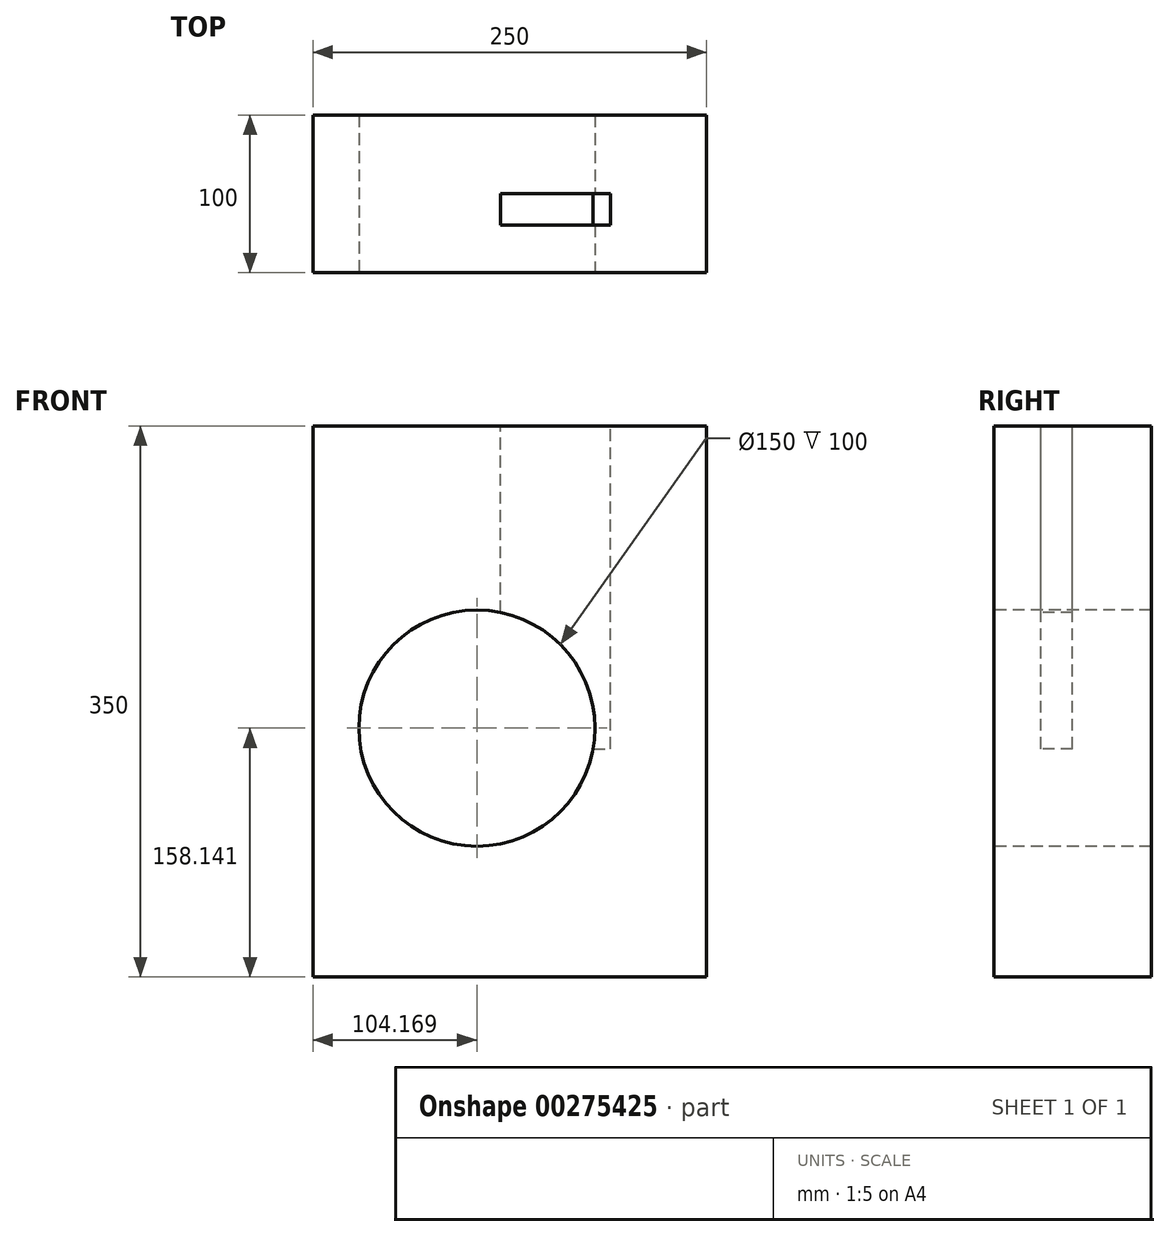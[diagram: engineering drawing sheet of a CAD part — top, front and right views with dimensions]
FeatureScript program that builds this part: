
annotation { "Feature Type Name" : "Feature", "Feature Type Description" : "" }
export const myFeature = defineFeature(function(context is Context, id is Id, definition is map)
    precondition{}
    {
        {
            var Q0;
            Q0=qCreatedBy(makeId("Front.planeOp"),FACE);
            var sketch = newSketch(context, id + "F0", { "sketchPlane" : qUnion([Q0])});
            skLineSegment(sketch, "E0.bottom", {"start": v(-125, 175) * mm, "end": v(125, 175) * mm});
            skLineSegment(sketch, "E0.top", {"start": v(-125, -175) * mm, "end": v(125, -175) * mm});
            skLineSegment(sketch, "E0.left", {"start": v(-125, 175) * mm, "end": v(-125, -175) * mm});
            skLineSegment(sketch, "E0.right", {"start": v(125, 175) * mm, "end": v(125, -175) * mm});
            skSolve(sketch);
        }
        {
            var Q0;
            Q0 = qSketchRegion(id + "F0", true);
            extrude(context, id + "F1", {"entities" : qUnion([Q0]), "depth" : 100 * mm});
        }
        {
            var Q0;
            Q0=makeQuery(id+"F1.opExtrude","CAP_FACE",FACE,{"disambiguationData":[OSD([sQuery(id+"F0.wireOp",EDGE,"E0.bottom"),sQuery(id+"F0.wireOp",EDGE,"E0.top"),sQuery(id+"F0.wireOp",EDGE,"E0.left"),sQuery(id+"F0.wireOp",EDGE,"E0.right")])],"isStart":false});
            var sketch = newSketch(context, id + "F2", { "sketchPlane" : qUnion([Q0])});
            skCircle(sketch, "E1", {"center": v(-20.83, -16.86) * mm, "radius": 75 * mm});
            skSolve(sketch);
        }
        {
            var Q0;
            Q0=makeQuery(id+"F2.imprint","IMPRINT",FACE,{"disambiguationData":[TD([[makeQuery(id+"F2.imprint","IMPRINT",EDGE,{"derivedFrom":sQuery(id+"F2.wireOp",EDGE,"E1")}),1.0]])]});
            extrude(context, id + "F3", {"entities" : qUnion([Q0]), "operationType" : NewBodyOperationType.REMOVE, "oppositeDirection" : true, "depth" : 267 * mm});
        }
        {
            var Q0;
            Q0=makeQuery(id+"F1.opExtrude","SWEPT_FACE",FACE,{"disambiguationData":[OSD([sQuery(id+"F0.wireOp",EDGE,"E0.bottom")])]});
            var sketch = newSketch(context, id + "F4", { "sketchPlane" : qUnion([Q0])});
            skLineSegment(sketch, "E2.bottom", {"start": v(-5.88, -50) * mm, "end": v(64.12, -50) * mm});
            skLineSegment(sketch, "E2.top", {"start": v(-5.88, -70) * mm, "end": v(64.12, -70) * mm});
            skLineSegment(sketch, "E2.left", {"start": v(-5.88, -50) * mm, "end": v(-5.88, -70) * mm});
            skLineSegment(sketch, "E2.right", {"start": v(64.12, -50) * mm, "end": v(64.12, -70) * mm});
            skSolve(sketch);
        }
        {
            var Q0;
            Q0 = qSketchRegion(id + "F4", true);
            extrude(context, id + "F5", {"entities" : qUnion([Q0]), "operationType" : NewBodyOperationType.REMOVE, "oppositeDirection" : true, "depth" : 205 * mm});
        }
    });
